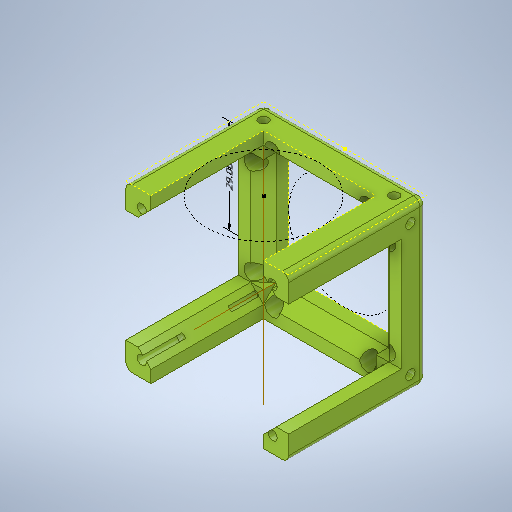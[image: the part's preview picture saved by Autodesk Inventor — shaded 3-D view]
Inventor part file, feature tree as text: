
AUTODESK INVENTOR PART (.ipt)
format: ipt  version: 2025.1 (Build 291241000, 241)  size: 589,824 bytes
history: native  units: mm
features: sketch x11, projected_geometry x9, hole x7, extrude x5, other x3, fillet x1, plane x1
ambient origin geometry x8: Origin, YZ Plane, XZ Plane, XY Plane, X Axis, Y Axis, Z Axis, Center Point
bodies: Solid1 (feature_tree)
feature tree (37):
  extrude  "Extrusion1"  Depth=49.8mm
  extrude  "Extrusion2"  Depth=7.7mm TaperAngle=0.0deg
  hole  "Hole1"  [1 undecoded]
  sketch  "Sketch4"  dims[d8=2.8mm d9=6.0mm d10=5.5mm d11=3.1mm d12=90.0deg d13=16.0mm d14=20.594885mm d23=2.0mm d30=33.8mm d31=0.0mm]
  sketch  "Sketch5"  dims[d35=33.8mm d36=0.0mm d37=54.2mm]
  other  "Work Axis1"
  other  "Work Axis2"
  fillet  "Fillet1"  Radius=33.8mm
  extrude  "Extrusion3"  Depth=54.2mm
  extrude  "Extrusion4"  Depth=54.2mm
  plane  "Work Plane1"
  extrude  "Extrusion5"  Depth=4.9mm
  hole  "Hole2"  [1 undecoded]
  hole  "Hole4"  [1 undecoded]
  hole  "Hole5"  [1 undecoded]
  hole  "Hole6"  [1 undecoded]
  hole  "Hole7"  [1 undecoded]
  hole  "Hole8"  [1 undecoded]
  sketch  "Sketch1"  dims[d0=49.8mm d1=49.8mm]
  sketch  "Sketch2"  dims[d2=7.7mm d3=7.7mm d4=0.0mm]
  projected_geometry  "Projected Loop1"
  sketch  "Sketch3"  dims[d5=34.4mm d6=0.0mm]
  projected_geometry  "Projected Loop3"
  projected_geometry  "Projected Loop4"
  projected_geometry  "Projected Loop5"
  projected_geometry  "Projected Loop6"
  projected_geometry  "Projected Loop7"
  sketch  "Sketch9"  dims[d38=135.0deg d39=54.2mm]
  sketch  "Sketch11"  dims[d40=33.8mm d41=0.0mm]
  projected_geometry  "Projected Loop11"
  sketch  "Sketch12"  dims[d42=2.8mm d43=6.0mm d44=3.0mm d45=2.0mm d46=90.0deg d47=12.0mm d48=20.594885mm]
  sketch  "Sketch13"  dims[d58=2.9mm d59=6.0mm d60=4.0mm d61=2.0mm d62=90.0deg d63=6.5mm d64=20.594885mm]
  sketch  "Sketch14"  dims[d67=2.9mm d68=6.0mm d69=4.0mm d70=2.0mm d71=90.0deg d72=6.5mm d73=20.594885mm]
  sketch  "Sketch15"  dims[d74=2.9mm d75=6.0mm d76=4.0mm d77=2.0mm d78=90.0deg d79=6.5mm d80=20.594885mm d81=2.9mm d82=6.0mm d83=4.0mm d84=2.0mm d85=90.0deg d86=6.5mm d87=20.594885mm d88=4.9mm d89=4.9mm d90=4.9mm d91=4.9mm d92=4.9mm d93=4.9mm d94=4.9mm d96=4.9mm d97=4.9mm d98=4.9mm d99=4.9mm d100=4.9mm d101=4.9mm d102=4.9mm d111=0.0mm d113=4.7mm d114=6.0mm d115=4.0mm d116=2.0mm d117=90.0deg d118=8.0mm d119=20.594885mm d120=54.2mm d121=54.2mm d122=54.0mm d123=54.0mm d124=29.0mm]
  projected_geometry  "Projected Loop13"
  projected_geometry  "Projected Loop14"
  other  "线性尺寸 1"
note: 7 required parameter values undecoded (feature->parameter linkage not recoverable at this tier; creation-order binding heuristic only, values carry confidence <= 0.55)
